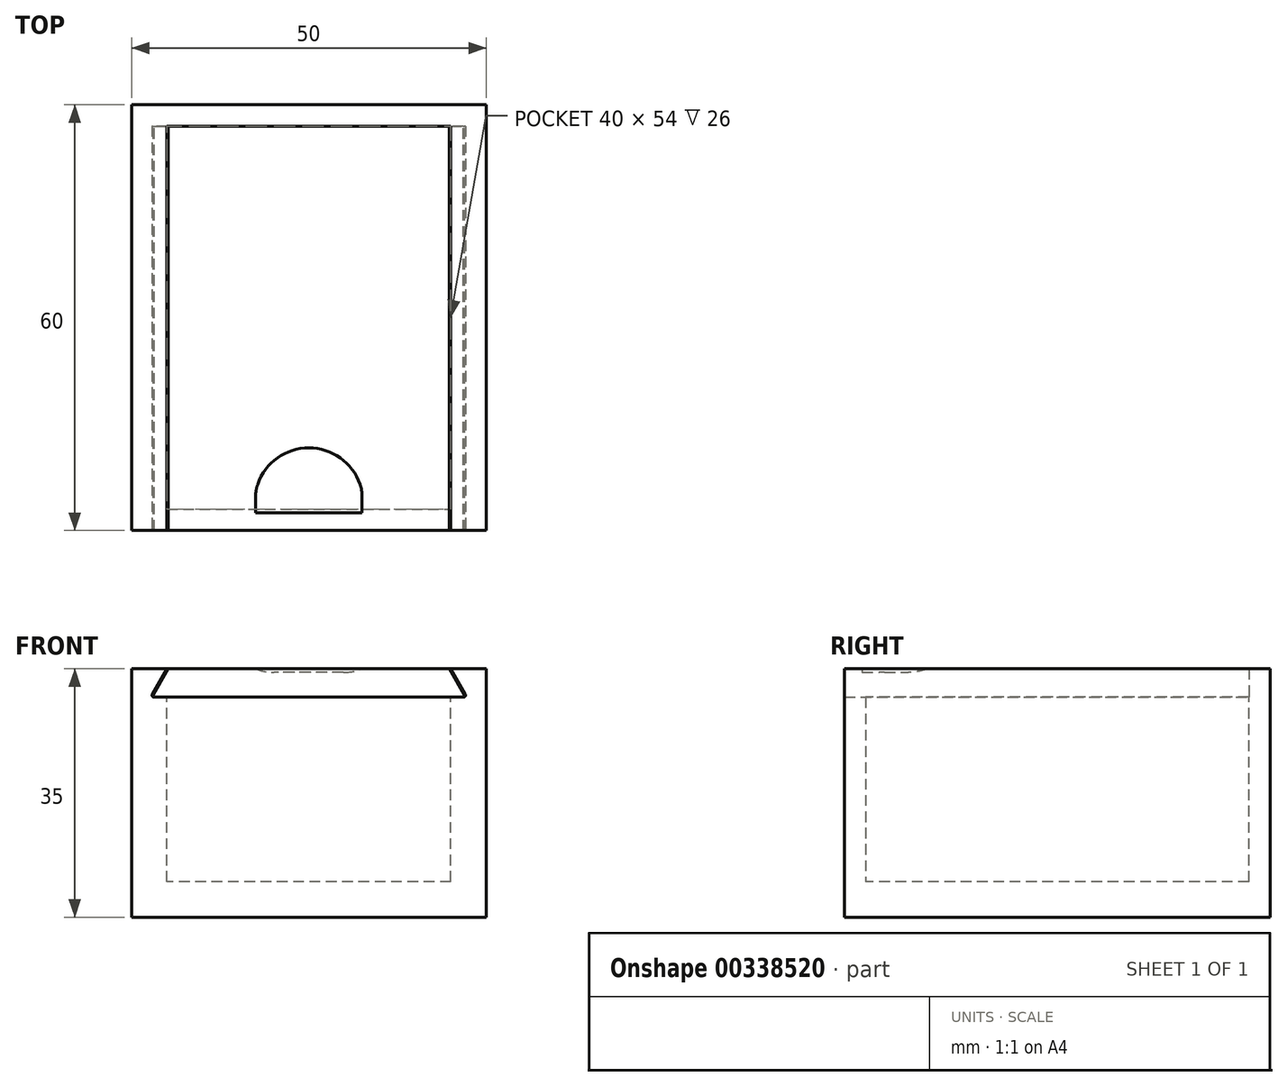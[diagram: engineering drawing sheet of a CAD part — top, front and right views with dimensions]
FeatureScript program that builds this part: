
annotation { "Feature Type Name" : "Feature", "Feature Type Description" : "" }
export const myFeature = defineFeature(function(context is Context, id is Id, definition is map)
    precondition{}
    {
        {
            var Q0;
            Q0=qCreatedBy(makeId("Front.planeOp"),FACE);
            var sketch = newSketch(context, id + "F0", { "sketchPlane" : qUnion([Q0])});
            skLineSegment(sketch, "E0.bottom", {"start": v(0, 0) * mm, "end": v(0, 0) * mm});
            skLineSegment(sketch, "E0.top", {"start": v(0, 0) * mm, "end": v(0, 0) * mm});
            skLineSegment(sketch, "E0.left", {"start": v(0, 0) * mm, "end": v(0, 0) * mm});
            skLineSegment(sketch, "E0.right", {"start": v(0, 0) * mm, "end": v(0, 0) * mm});
            skPoint(sketch, "E0.middle", {"position": v(0, 0) * mm});
            skLineSegment(sketch, "E1.bottom", {"start": v(0, -15) * mm, "end": v(-25, -15) * mm});
            skLineSegment(sketch, "E1.right", {"start": v(-25, -15) * mm, "end": v(-25, 20) * mm});
            skLineSegment(sketch, "E2.0", {"start": v(-20, -10) * mm, "end": v(-20, 16) * mm});
            skLineSegment(sketch, "E2.1", {"start": v(0, -10) * mm, "end": v(-20, -10) * mm});
            skLineSegment(sketch, "E3.trimOffspring", {"start": v(-20, 20) * mm, "end": v(-25, 20) * mm});
            skLineSegment(sketch, "E4", {"start": v(-20, 20) * mm, "end": v(-22.05, 16.45) * mm});
            skLineSegment(sketch, "E5", {"start": v(-22.3, 16) * mm, "end": v(-22.3, 16) * mm});
            skLineSegment(sketch, "E6", {"start": v(-21.79, 16) * mm, "end": v(-20, 16) * mm});
            skLineSegment(sketch, "E7", {"start": v(0, -10) * mm, "end": v(0, -15) * mm});
            skPoint(sketch, "E2.2.start.orphan", {"position": v(15.06, -27.88) * mm});
            skPoint(sketch, "E1.left.start.orphan", {"position": v(20.06, -32.88) * mm});
            skPoint(sketch, "E1.top.start.orphan", {"position": v(25, 19) * mm});
            skPoint(sketch, "E8.visualSharp", {"position": v(-22.3, 16) * mm});
            skArc(sketch, "E8.filletArc", {"start": v(-22.05, 16.45) * mm, "mid": v(-22.05, 16.15) * mm, "end": v(-21.79, 16) * mm});
            skLineSegment(sketch, "E9", {"start": v(0, -4.99) * mm, "end": v(0, 8.01) * mm, "construction": true});
            skLineSegment(sketch, "E10.MirrorCS", {"start": v(20, -10) * mm, "end": v(20, 16) * mm});
            skLineSegment(sketch, "E11.MirrorCS", {"start": v(25, -15) * mm, "end": v(25, 20) * mm});
            skLineSegment(sketch, "E12.MirrorCS", {"start": v(20, 20) * mm, "end": v(25, 20) * mm});
            skLineSegment(sketch, "E13.MirrorCS", {"start": v(20, 20) * mm, "end": v(22.05, 16.45) * mm});
            skArc(sketch, "E14.MirrorCS", {"start": v(22.05, 16.45) * mm, "mid": v(22.05, 16.15) * mm, "end": v(21.79, 16) * mm});
            skLineSegment(sketch, "E15.MirrorCS", {"start": v(21.79, 16) * mm, "end": v(20, 16) * mm});
            skLineSegment(sketch, "E16.MirrorCS", {"start": v(0, -10) * mm, "end": v(20, -10) * mm});
            skLineSegment(sketch, "E17.MirrorCS", {"start": v(0, -15) * mm, "end": v(25, -15) * mm});
            skPoint(sketch, "E18.orphan", {"position": v(-20, 18) * mm});
            skPoint(sketch, "E19.MirrorCS.end.orphan", {"position": v(20, 20) * mm});
            skPoint(sketch, "E19.MirrorCS.start.orphan", {"position": v(20, 18) * mm});
            skLineSegment(sketch, "E20.2", {"start": v(-19.8, 20) * mm, "end": v(-21.92, 16.37) * mm});
            skLineSegment(sketch, "E21", {"start": v(-20, 20) * mm, "end": v(-19.8, 20) * mm, "construction": true});
            skArc(sketch, "E22", {"start": v(-21.92, 16.37) * mm, "mid": v(-21.94, 16.16) * mm, "end": v(-21.79, 16) * mm});
            skLineSegment(sketch, "E23", {"start": v(-20, 16) * mm, "end": v(0, 16) * mm});
            skLineSegment(sketch, "E24", {"start": v(-19.8, 20) * mm, "end": v(0, 20) * mm});
            skLineSegment(sketch, "E25.MirrorCS", {"start": v(19.8, 20) * mm, "end": v(0, 20) * mm});
            skLineSegment(sketch, "E26.MirrorCS", {"start": v(20, 16) * mm, "end": v(0, 16) * mm});
            skLineSegment(sketch, "E27.MirrorCS", {"start": v(19.8, 20) * mm, "end": v(21.92, 16.37) * mm});
            skArc(sketch, "E28.MirrorCS", {"start": v(21.92, 16.37) * mm, "mid": v(21.94, 16.16) * mm, "end": v(21.79, 16) * mm});
            skSolve(sketch);
        }
        {
            var Q0;
            Q0=makeQuery(id+"F0.imprint","IMPRINT",FACE,{"disambiguationData":[TD([[makeQuery(id+"F0.imprint","IMPRINT",EDGE,{"derivedFrom":sQuery(id+"F0.wireOp",EDGE,"E1.bottom")}),-1.0]])]});
            var Q1;
            Q1=makeQuery(id+"F0.imprint","IMPRINT",FACE,{"disambiguationData":[TD([[makeQuery(id+"F0.imprint","IMPRINT",EDGE,{"derivedFrom":sQuery(id+"F0.wireOp",EDGE,"E7")}),1.0]])]});
            extrude(context, id + "F1", {"entities" : qUnion([Q0, Q1]), "oppositeDirection" : true, "depth" : 30 * mm, "hasSecondDirection" : true, "secondDirectionOppositeDirection" : false, "secondDirectionDepth" : 30 * mm});
        }
        {
            var Q0;
            Q0=makeQuery(id+"F1.opExtrude","CAP_FACE",FACE,{"disambiguationData":[OSD([sQuery(id+"F0.wireOp",EDGE,"E1.bottom"),sQuery(id+"F0.wireOp",EDGE,"E1.right"),sQuery(id+"F0.wireOp",EDGE,"E2.0"),sQuery(id+"F0.wireOp",EDGE,"E2.1"),sQuery(id+"F0.wireOp",EDGE,"E3.trimOffspring"),sQuery(id+"F0.wireOp",EDGE,"E4"),sQuery(id+"F0.wireOp",EDGE,"E6"),sQuery(id+"F0.wireOp",EDGE,"E8.filletArc"),sQuery(id+"F0.wireOp",EDGE,"E10.MirrorCS"),sQuery(id+"F0.wireOp",EDGE,"E11.MirrorCS"),sQuery(id+"F0.wireOp",EDGE,"E12.MirrorCS"),sQuery(id+"F0.wireOp",EDGE,"E13.MirrorCS"),sQuery(id+"F0.wireOp",EDGE,"E14.MirrorCS"),sQuery(id+"F0.wireOp",EDGE,"E15.MirrorCS"),sQuery(id+"F0.wireOp",EDGE,"E16.MirrorCS"),sQuery(id+"F0.wireOp",EDGE,"E17.MirrorCS")])],"isStart":true});
            var sketch = newSketch(context, id + "F2", { "sketchPlane" : qUnion([Q0])});
            skLineSegment(sketch, "E29", {"start": v(-25, 16) * mm, "end": v(25, 16) * mm});
            skLineSegment(sketch, "E30", {"start": v(-25, 16) * mm, "end": v(-25, -15) * mm});
            skLineSegment(sketch, "E31", {"start": v(-25, -15) * mm, "end": v(-25, -15) * mm});
            skLineSegment(sketch, "E32", {"start": v(-25, -15) * mm, "end": v(25, -15) * mm});
            skLineSegment(sketch, "E33", {"start": v(25, -15) * mm, "end": v(25, -15) * mm});
            skLineSegment(sketch, "E34", {"start": v(25, 16) * mm, "end": v(25, -15) * mm});
            skSolve(sketch);
        }
        {
            var Q0;
            {var subQ1=makeQuery(id+"F1.opExtrude","CAP_EDGE",EDGE,{"disambiguationData":[OSD([sQuery(id+"F0.wireOp",EDGE,"E2.0")])],"isStart":true});Q0=makeQuery(id+"F2.imprint","IMPRINT",FACE,{"disambiguationData":[TD([[makeQuery(id+"F2.imprint","IMPRINT",EDGE,{"derivedFrom":subQ1}),-1.0]])]});}
            var Q1;
            {var subQ6=sQuery(id+"F2.wireOp",EDGE,"E30");Q1=makeQuery(id+"F2.imprint","IMPRINT",FACE,{"disambiguationData":[TD([[makeQuery(id+"F2.imprint","IMPRINT",EDGE,{"derivedFrom":subQ6}),-1.0]])]});}
            extrude(context, id + "F3", {"entities" : qUnion([Q0, Q1]), "operationType" : NewBodyOperationType.ADD, "oppositeDirection" : true, "depth" : 3 * mm});
        }
        {
            var Q0;
            Q0=makeQuery(id+"F1.opExtrude","CAP_FACE",FACE,{"disambiguationData":[OSD([sQuery(id+"F0.wireOp",EDGE,"E1.bottom"),sQuery(id+"F0.wireOp",EDGE,"E1.right"),sQuery(id+"F0.wireOp",EDGE,"E2.0"),sQuery(id+"F0.wireOp",EDGE,"E2.1"),sQuery(id+"F0.wireOp",EDGE,"E3.trimOffspring"),sQuery(id+"F0.wireOp",EDGE,"E4"),sQuery(id+"F0.wireOp",EDGE,"E6"),sQuery(id+"F0.wireOp",EDGE,"E8.filletArc"),sQuery(id+"F0.wireOp",EDGE,"E10.MirrorCS"),sQuery(id+"F0.wireOp",EDGE,"E11.MirrorCS"),sQuery(id+"F0.wireOp",EDGE,"E12.MirrorCS"),sQuery(id+"F0.wireOp",EDGE,"E13.MirrorCS"),sQuery(id+"F0.wireOp",EDGE,"E14.MirrorCS"),sQuery(id+"F0.wireOp",EDGE,"E15.MirrorCS"),sQuery(id+"F0.wireOp",EDGE,"E16.MirrorCS"),sQuery(id+"F0.wireOp",EDGE,"E17.MirrorCS")])],"isStart":false});
            var sketch = newSketch(context, id + "F4", { "sketchPlane" : qUnion([Q0])});
            skLineSegment(sketch, "E35", {"start": v(-25, 20) * mm, "end": v(-25, -15) * mm});
            skLineSegment(sketch, "E36", {"start": v(-25, -15) * mm, "end": v(-25, -15) * mm});
            skLineSegment(sketch, "E37", {"start": v(-25, -15) * mm, "end": v(25, -15) * mm});
            skLineSegment(sketch, "E38", {"start": v(25, -15) * mm, "end": v(25, -15) * mm});
            skLineSegment(sketch, "E39", {"start": v(25, 20) * mm, "end": v(25, -15) * mm});
            skLineSegment(sketch, "E40", {"start": v(25, 20) * mm, "end": v(-25, 20) * mm});
            skSolve(sketch);
        }
        {
            var Q0;
            Q0=makeQuery(id+"F4.imprint","IMPRINT",FACE,{"disambiguationData":[TD([[makeQuery(id+"F4.imprint","IMPRINT",EDGE,{"derivedFrom":makeQuery(id+"F1.opExtrude","CAP_EDGE",EDGE,{"disambiguationData":[OSD([sQuery(id+"F0.wireOp",EDGE,"E2.0")])],"isStart":false})}),1.0]])]});
            extrude(context, id + "F5", {"entities" : qUnion([Q0]), "operationType" : NewBodyOperationType.ADD, "oppositeDirection" : true, "depth" : 3 * mm});
        }
        {
            var Q0;
            Q0=makeQuery(id+"F0.imprint","IMPRINT",FACE,{"disambiguationData":[TD([[makeQuery(id+"F0.imprint","IMPRINT",EDGE,{"derivedFrom":sQuery(id+"F0.wireOp",EDGE,"E6")}),1.0]])]});
            extrude(context, id + "F6", {"entities" : qUnion([Q0]), "depth" : 30 * mm, "hasSecondDirection" : true, "secondDirectionOppositeDirection" : true, "secondDirectionDepth" : 27 * mm});
        }
        {
            var Q0;
            Q0=makeQuery(id+"F6.opExtrude","SWEPT_FACE",FACE,{"disambiguationData":[OSD([sQuery(id+"F0.wireOp",EDGE,"E24"),sQuery(id+"F0.wireOp",EDGE,"E25.MirrorCS")])]});
            var sketch = newSketch(context, id + "F7", { "sketchPlane" : qUnion([Q0])});
            skLineSegment(sketch, "E41.bottom", {"start": v(7.5, -24.5) * mm, "end": v(-7.5, -24.5) * mm, "construction": true});
            skLineSegment(sketch, "E41.top", {"start": v(7.5, -27.5) * mm, "end": v(-7.5, -27.5) * mm});
            skLineSegment(sketch, "E41.left", {"start": v(7.5, -25.13) * mm, "end": v(7.5, -27.5) * mm});
            skLineSegment(sketch, "E41.right", {"start": v(-7.5, -25.13) * mm, "end": v(-7.5, -27.5) * mm});
            skPoint(sketch, "E41.middle", {"position": v(0, -26) * mm});
            skArc(sketch, "E42", {"start": v(7.22, -23.47) * mm, "mid": v(0, -18.35) * mm, "end": v(-7.22, -23.47) * mm});
            skPoint(sketch, "E43.visualSharp", {"position": v(-7.5, -24.5) * mm});
            skArc(sketch, "E43.filletArc", {"start": v(-7.22, -23.47) * mm, "mid": v(-7.43, -24.29) * mm, "end": v(-7.5, -25.13) * mm});
            skPoint(sketch, "E44.visualSharp", {"position": v(7.5, -24.5) * mm});
            skArc(sketch, "E44.filletArc", {"start": v(7.5, -25.13) * mm, "mid": v(7.43, -24.29) * mm, "end": v(7.22, -23.47) * mm});
            skSolve(sketch);
        }
        {
            var Q0;
            Q0=makeQuery(id+"F7.imprint","IMPRINT",FACE,{"disambiguationData":[TD([[makeQuery(id+"F7.imprint","IMPRINT",EDGE,{"derivedFrom":sQuery(id+"F7.wireOp",EDGE,"E41.bottom")}),1.0]])]});
            var Q1;
            Q1=makeQuery(id+"F7.imprint","IMPRINT",FACE,{"disambiguationData":[TD([[makeQuery(id+"F7.imprint","IMPRINT",EDGE,{"derivedFrom":sQuery(id+"F7.wireOp",EDGE,"E41.top")}),-1.0]])]});
            extrude(context, id + "F8", {"entities" : qUnion([Q0, Q1]), "operationType" : NewBodyOperationType.REMOVE, "oppositeDirection" : true, "depth" : 0.5 * mm});
        }
        {
            var Q0;
            Q0=makeQuery(id+"F8.boolean.opBoolean","COPY",EDGE,{"derivedFrom":makeQuery(id+"F8.opExtrude","CAP_EDGE",EDGE,{"disambiguationData":[OSD([sQuery(id+"F7.wireOp",EDGE,"E42")])],"isStart":false})});
            fillet(context, id + "F9", {"entities" : qUnion([Q0]), "radius" : 7 * mm, "tangentPropagation" : true, "allowEdgeOverflow" : false});
        }
    });
